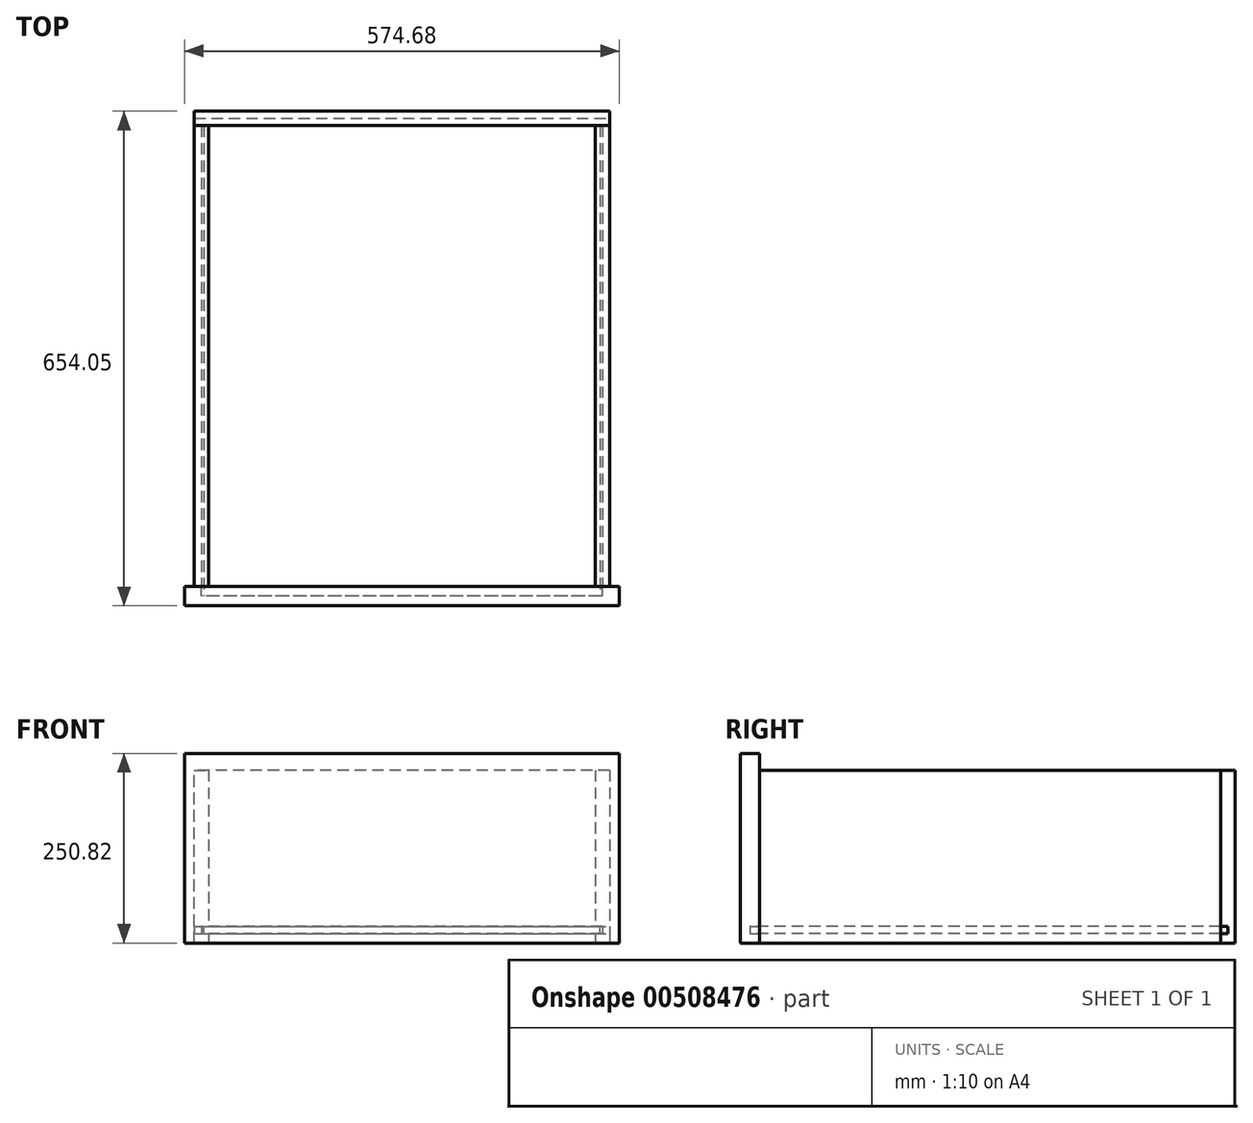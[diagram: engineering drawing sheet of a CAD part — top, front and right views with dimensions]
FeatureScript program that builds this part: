
annotation { "Feature Type Name" : "Feature", "Feature Type Description" : "" }
export const myFeature = defineFeature(function(context is Context, id is Id, definition is map)
    precondition{}
    {
        {
            var Q0;
            Q0=qCreatedBy(makeId("Front.planeOp"),FACE);
            var sketch = newSketch(context, id + "F0", { "sketchPlane" : qUnion([Q0])});
            skLineSegment(sketch, "E0.bottom", {"start": v(-287.34, 125.41) * mm, "end": v(287.34, 125.41) * mm});
            skLineSegment(sketch, "E0.top", {"start": v(-287.34, -125.41) * mm, "end": v(287.34, -125.41) * mm});
            skLineSegment(sketch, "E0.left", {"start": v(-287.34, 125.41) * mm, "end": v(-287.34, -125.41) * mm});
            skLineSegment(sketch, "E0.right", {"start": v(287.34, 125.41) * mm, "end": v(287.34, -125.41) * mm});
            skSolve(sketch);
        }
        {
            var Q0;
            Q0=makeQuery(id+"F0.imprint","IMPRINT",FACE,{"disambiguationData":[TD([[makeQuery(id+"F0.imprint","IMPRINT",EDGE,{"derivedFrom":sQuery(id+"F0.wireOp",EDGE,"E0.bottom")}),-1.0]])]});
            extrude(context, id + "F1", {"entities" : qUnion([Q0]), "depth" : 25.4 * mm});
        }
        {
            var Q0;
            Q0=makeQuery(id+"F1.opExtrude","CAP_FACE",FACE,{"disambiguationData":[OSD([sQuery(id+"F0.wireOp",EDGE,"E0.bottom"),sQuery(id+"F0.wireOp",EDGE,"E0.top"),sQuery(id+"F0.wireOp",EDGE,"E0.left"),sQuery(id+"F0.wireOp",EDGE,"E0.right")])],"isStart":true});
            var sketch = newSketch(context, id + "F2", { "sketchPlane" : qUnion([Q0])});
            skLineSegment(sketch, "E1.bottom", {"start": v(-274.64, 103.19) * mm, "end": v(-255.59, 103.19) * mm});
            skLineSegment(sketch, "E1.top", {"start": v(-274.64, -125.41) * mm, "end": v(-255.59, -125.41) * mm});
            skLineSegment(sketch, "E1.right", {"start": v(-255.59, 103.19) * mm, "end": v(-255.59, -103.19) * mm});
            skLineSegment(sketch, "E2.bottom", {"start": v(274.64, 103.19) * mm, "end": v(255.59, 103.19) * mm});
            skLineSegment(sketch, "E2.top", {"start": v(274.64, -125.41) * mm, "end": v(255.59, -125.41) * mm});
            skLineSegment(sketch, "E2.right", {"start": v(255.59, 103.19) * mm, "end": v(255.59, -103.19) * mm});
            skLineSegment(sketch, "E3.bottom", {"start": v(265.11, -103.19) * mm, "end": v(255.59, -103.19) * mm});
            skLineSegment(sketch, "E3.top", {"start": v(265.11, -112.71) * mm, "end": v(255.59, -112.71) * mm});
            skLineSegment(sketch, "E4", {"start": v(-265.11, -102.9) * mm, "end": v(-265.11, -112.71) * mm});
            skLineSegment(sketch, "E5", {"start": v(265.11, -103.19) * mm, "end": v(265.11, -112.71) * mm});
            skLineSegment(sketch, "E6.trimOffspring", {"start": v(-255.59, -103.19) * mm, "end": v(-265.11, -103.19) * mm});
            skLineSegment(sketch, "E7.trimOffspring", {"start": v(-255.59, -112.71) * mm, "end": v(-265.11, -112.71) * mm});
            skLineSegment(sketch, "E8.trimOffspring", {"start": v(-255.59, -112.71) * mm, "end": v(-255.59, -125.41) * mm});
            skLineSegment(sketch, "E9.trimOffspring", {"start": v(255.59, -112.71) * mm, "end": v(255.59, -125.41) * mm});
            skLineSegment(sketch, "E10", {"start": v(-274.64, 103.19) * mm, "end": v(-274.64, -125.41) * mm});
            skLineSegment(sketch, "E11", {"start": v(274.64, 103.19) * mm, "end": v(274.64, -125.41) * mm});
            skSolve(sketch);
        }
        {
            var Q0;
            Q0=qSketchRegion(id+"F2",true);
            extrude(context, id + "F3", {"entities" : qUnion([Q0]), "depth" : 609.6 * mm});
        }
        {
            var Q0;
            Q0=makeQuery(id+"F1.opExtrude","CAP_FACE",FACE,{"disambiguationData":[OSD([sQuery(id+"F0.wireOp",EDGE,"E0.bottom"),sQuery(id+"F0.wireOp",EDGE,"E0.top"),sQuery(id+"F0.wireOp",EDGE,"E0.left"),sQuery(id+"F0.wireOp",EDGE,"E0.right")])],"isStart":true});
            var sketch = newSketch(context, id + "F4", { "sketchPlane" : qUnion([Q0])});
            skLineSegment(sketch, "E12.bottom", {"start": v(-265.11, -103.19) * mm, "end": v(265.11, -103.19) * mm});
            skLineSegment(sketch, "E12.top", {"start": v(-265.11, -112.71) * mm, "end": v(265.11, -112.71) * mm});
            skLineSegment(sketch, "E12.left", {"start": v(-265.11, -103.19) * mm, "end": v(-265.11, -112.71) * mm});
            skLineSegment(sketch, "E12.right", {"start": v(265.11, -103.19) * mm, "end": v(265.11, -112.71) * mm});
            skSolve(sketch);
        }
        {
            var Q0;
            Q0=qSketchRegion(id+"F4",true);
            extrude(context, id + "F5", {"entities" : qUnion([Q0]), "operationType" : NewBodyOperationType.REMOVE, "oppositeDirection" : true, "depth" : 12.7 * mm});
        }
        {
            var Q0;
            Q0=makeQuery(id+"F5.boolean.opBoolean","COPY",FACE,{"derivedFrom":makeQuery(id+"F5.opExtrude","CAP_FACE",FACE,{"disambiguationData":[OSD([sQuery(id+"F4.wireOp",EDGE,"E12.bottom"),sQuery(id+"F4.wireOp",EDGE,"E12.top"),sQuery(id+"F4.wireOp",EDGE,"E12.left"),sQuery(id+"F4.wireOp",EDGE,"E12.right")])],"isStart":false})});
            var sketch = newSketch(context, id + "F6", { "sketchPlane" : qUnion([Q0])});
            skLineSegment(sketch, "E13.bottom", {"start": v(-261.94, -103.19) * mm, "end": v(261.94, -103.19) * mm});
            skLineSegment(sketch, "E13.top", {"start": v(-261.94, -112.71) * mm, "end": v(261.94, -112.71) * mm});
            skLineSegment(sketch, "E13.left", {"start": v(-261.94, -103.19) * mm, "end": v(-261.94, -112.71) * mm});
            skLineSegment(sketch, "E13.right", {"start": v(261.94, -103.19) * mm, "end": v(261.94, -112.71) * mm});
            skSolve(sketch);
        }
        {
            var Q0;
            Q0=makeQuery(id+"F6.imprint","IMPRINT",FACE,{"disambiguationData":[TD([[makeQuery(id+"F6.imprint","IMPRINT",EDGE,{"derivedFrom":sQuery(id+"F6.wireOp",EDGE,"E13.bottom")}),-1.0]])]});
            extrude(context, id + "F7", {"entities" : qUnion([Q0]), "depth" : 628.65 * mm});
        }
        {
            var Q0;
            Q0=makeQuery(id+"F3.opExtrude","CAP_FACE",FACE,{"disambiguationData":[OSD([sQuery(id+"F2.wireOp",EDGE,"E1.bottom"),sQuery(id+"F2.wireOp",EDGE,"E1.top"),sQuery(id+"F2.wireOp",EDGE,"E1.left"),sQuery(id+"F2.wireOp",EDGE,"E1.right"),sQuery(id+"F2.wireOp",EDGE,"E4"),sQuery(id+"F2.wireOp",EDGE,"E6.trimOffspring"),sQuery(id+"F2.wireOp",EDGE,"E7.trimOffspring"),sQuery(id+"F2.wireOp",EDGE,"E8.trimOffspring")])],"isStart":false});
            var sketch = newSketch(context, id + "F8", { "sketchPlane" : qUnion([Q0])});
            skLineSegment(sketch, "E14.bottom", {"start": v(-274.64, -125.41) * mm, "end": v(274.64, -125.41) * mm});
            skLineSegment(sketch, "E14.top", {"start": v(-274.64, 103.19) * mm, "end": v(274.64, 103.19) * mm});
            skLineSegment(sketch, "E14.left", {"start": v(-274.64, -125.41) * mm, "end": v(-274.64, 103.19) * mm});
            skLineSegment(sketch, "E14.right", {"start": v(274.64, -125.41) * mm, "end": v(274.64, 103.19) * mm});
            skSolve(sketch);
        }
        {
            var Q0;
            Q0=qSketchRegion(id+"F8",true);
            extrude(context, id + "F9", {"entities" : qUnion([Q0]), "depth" : 19.05 * mm});
        }
        {
            var Q0;
            Q0=makeQuery(id+"F9.opExtrude","SWEPT_FACE",FACE,{"disambiguationData":[OSD([sQuery(id+"F8.wireOp",EDGE,"E14.left")])]});
            var sketch = newSketch(context, id + "F10", { "sketchPlane" : qUnion([Q0])});
            skLineSegment(sketch, "E15.bottom", {"start": v(609.6, -103.19) * mm, "end": v(619.12, -103.19) * mm});
            skLineSegment(sketch, "E15.top", {"start": v(609.6, -112.71) * mm, "end": v(619.12, -112.71) * mm});
            skLineSegment(sketch, "E15.left", {"start": v(609.6, -103.19) * mm, "end": v(609.6, -112.71) * mm});
            skLineSegment(sketch, "E15.right", {"start": v(619.12, -103.19) * mm, "end": v(619.12, -112.71) * mm});
            skSolve(sketch);
        }
        {
            var Q0;
            Q0=qSketchRegion(id+"F10",true);
            extrude(context, id + "F11", {"entities" : qUnion([Q0]), "operationType" : NewBodyOperationType.REMOVE, "oppositeDirection" : true, "depth" : 584.2 * mm});
        }
    });
